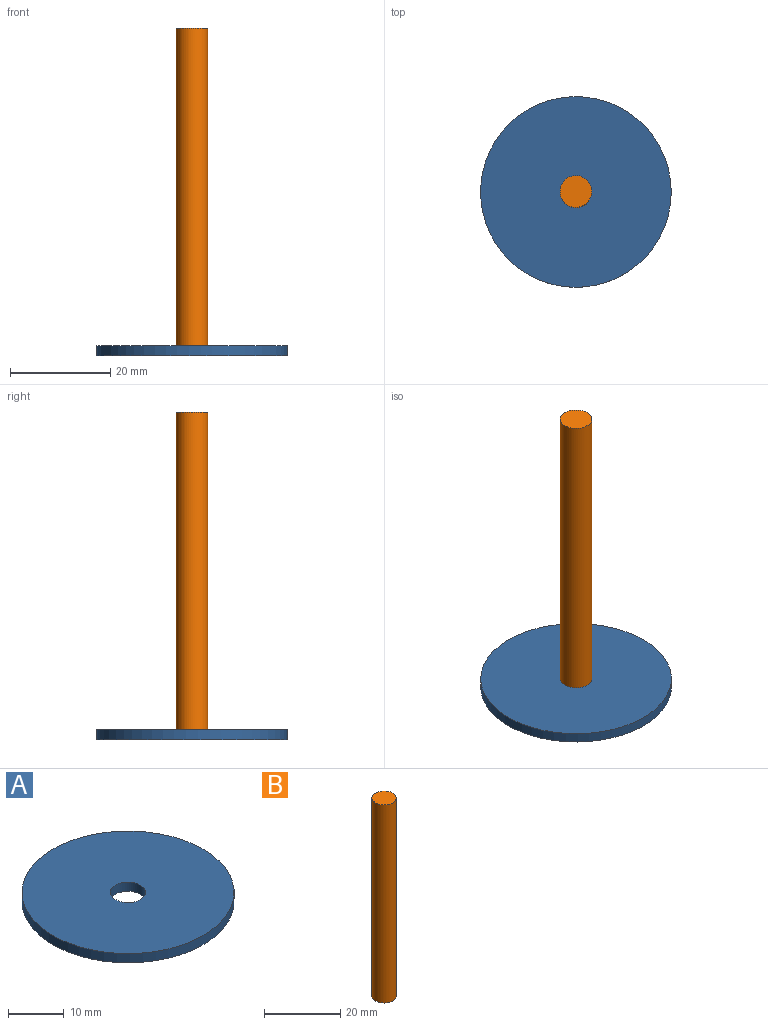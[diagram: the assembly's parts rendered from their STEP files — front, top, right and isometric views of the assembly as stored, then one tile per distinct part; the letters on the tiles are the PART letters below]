
ASSEMBLY  parts=2 mates=1
PART A: 4 faces, bbox 38.1x38.1x2 mm
  f0: cylinder r=3.17mm len=6.35mm, axis (0,0,-1), area 40.5mm2, adj f2,f3
  f1: cylinder r=19.05mm len=38.1mm, axis (0,0,-1), area 243.2mm2, adj f2,f3
  f2: plane 38.1x38.1mm, normal (0,0,1), area 1108.4mm2, adj f0,f1
  f3: plane 38.1x38.1mm, normal (0,0,-1), area 1108.4mm2, adj f0,f1
PART B: 3 faces, bbox 6.4x6.4x63.5 mm
  f0: plane 6.35x6.35mm, normal (0,0,1), area 31.7mm2, adj f1
  f1: cylinder r=3.17mm len=63.5mm, axis (0,0,-1), area 1266.8mm2, adj f0,f2
  f2: plane 6.35x6.35mm, normal (0,0,-1), area 31.7mm2, adj f1
PLACE A t=(69.85,0,-71.88)mm
PLACE B t=(69.85,0,-69.85)mm
MATE fastened B.f1 <-> A.f1  axis (0,0,-1) through (0,0,0)mm
